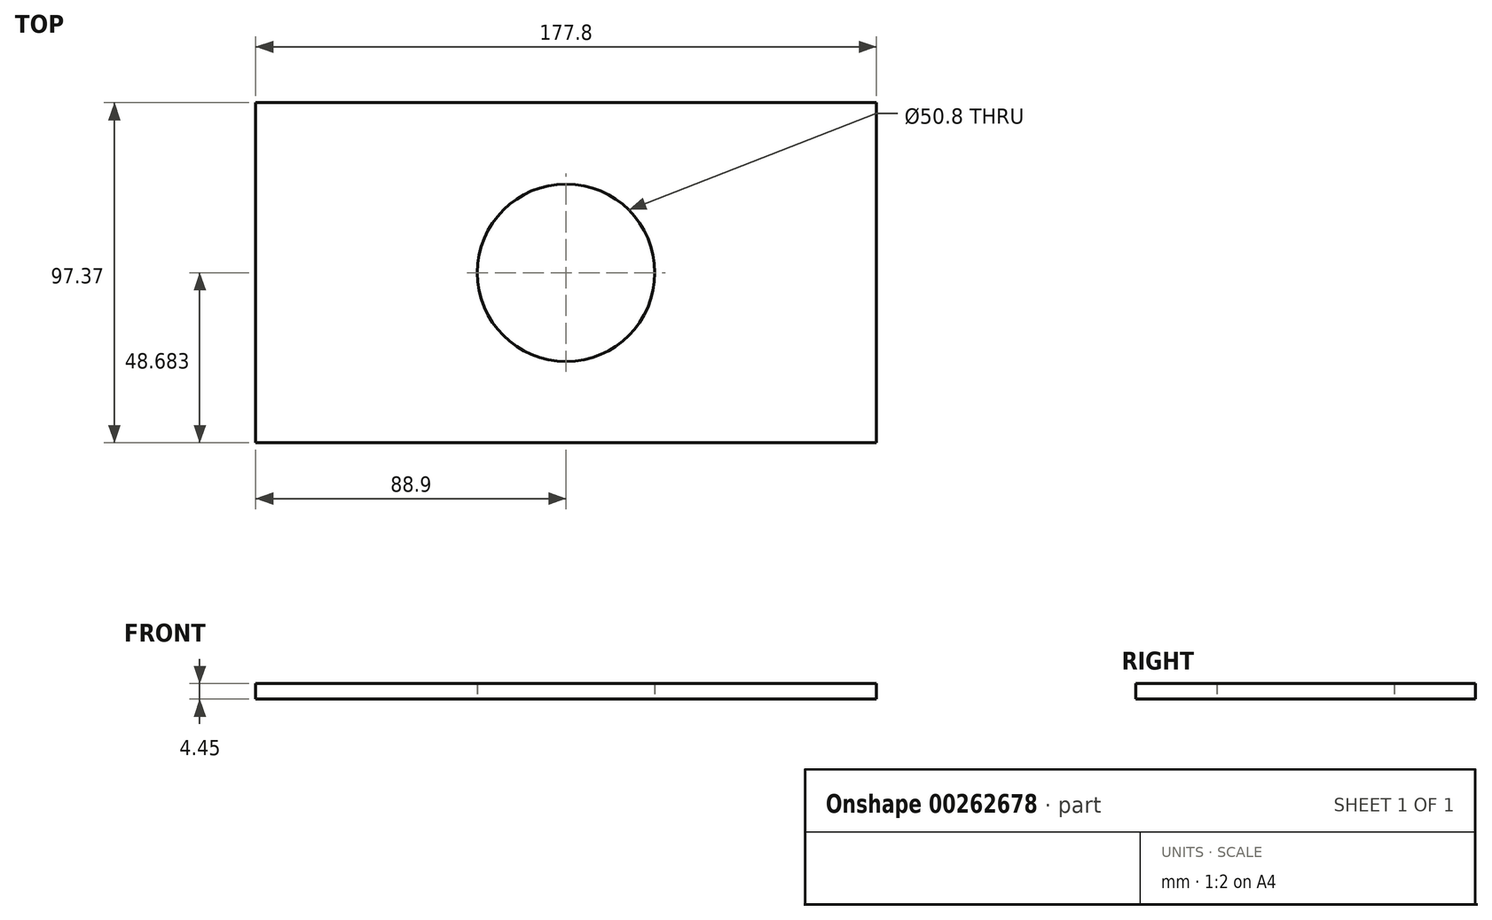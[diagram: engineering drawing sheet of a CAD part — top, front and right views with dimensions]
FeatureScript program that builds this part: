
annotation { "Feature Type Name" : "Feature", "Feature Type Description" : "" }
export const myFeature = defineFeature(function(context is Context, id is Id, definition is map)
    precondition{}
    {
        {
            var Q0;
            Q0=qCreatedBy(makeId("Top.planeOp"),FACE);
            var sketch = newSketch(context, id + "F0", { "sketchPlane" : qUnion([Q0])});
            skLineSegment(sketch, "E0.bottom", {"start": v(0, 0) * mm, "end": v(177.8, 0) * mm});
            skLineSegment(sketch, "E0.top", {"start": v(0, 97.37) * mm, "end": v(177.8, 97.37) * mm});
            skLineSegment(sketch, "E0.left", {"start": v(0, 0) * mm, "end": v(0, 97.37) * mm});
            skLineSegment(sketch, "E0.right", {"start": v(177.8, 0) * mm, "end": v(177.8, 97.37) * mm});
            skCircle(sketch, "E1", {"center": v(88.9, 48.68) * mm, "radius": 25.4 * mm});
            skPoint(sketch, "E1.centerSnap0", {"position": v(88.9, 0) * mm});
            skPoint(sketch, "E1.centerSnap1", {"position": v(0, 48.68) * mm});
            skSolve(sketch);
        }
        {
            var Q0;
            Q0=makeQuery(id+"F0.imprint","IMPRINT",FACE,{"disambiguationData":[TD([[makeQuery(id+"F0.imprint","IMPRINT",EDGE,{"derivedFrom":sQuery(id+"F0.wireOp",EDGE,"E0.bottom")}),1.0]])]});
            extrude(context, id + "F1", {"entities" : qUnion([Q0]), "depth" : 4.44 * mm});
        }
    });
